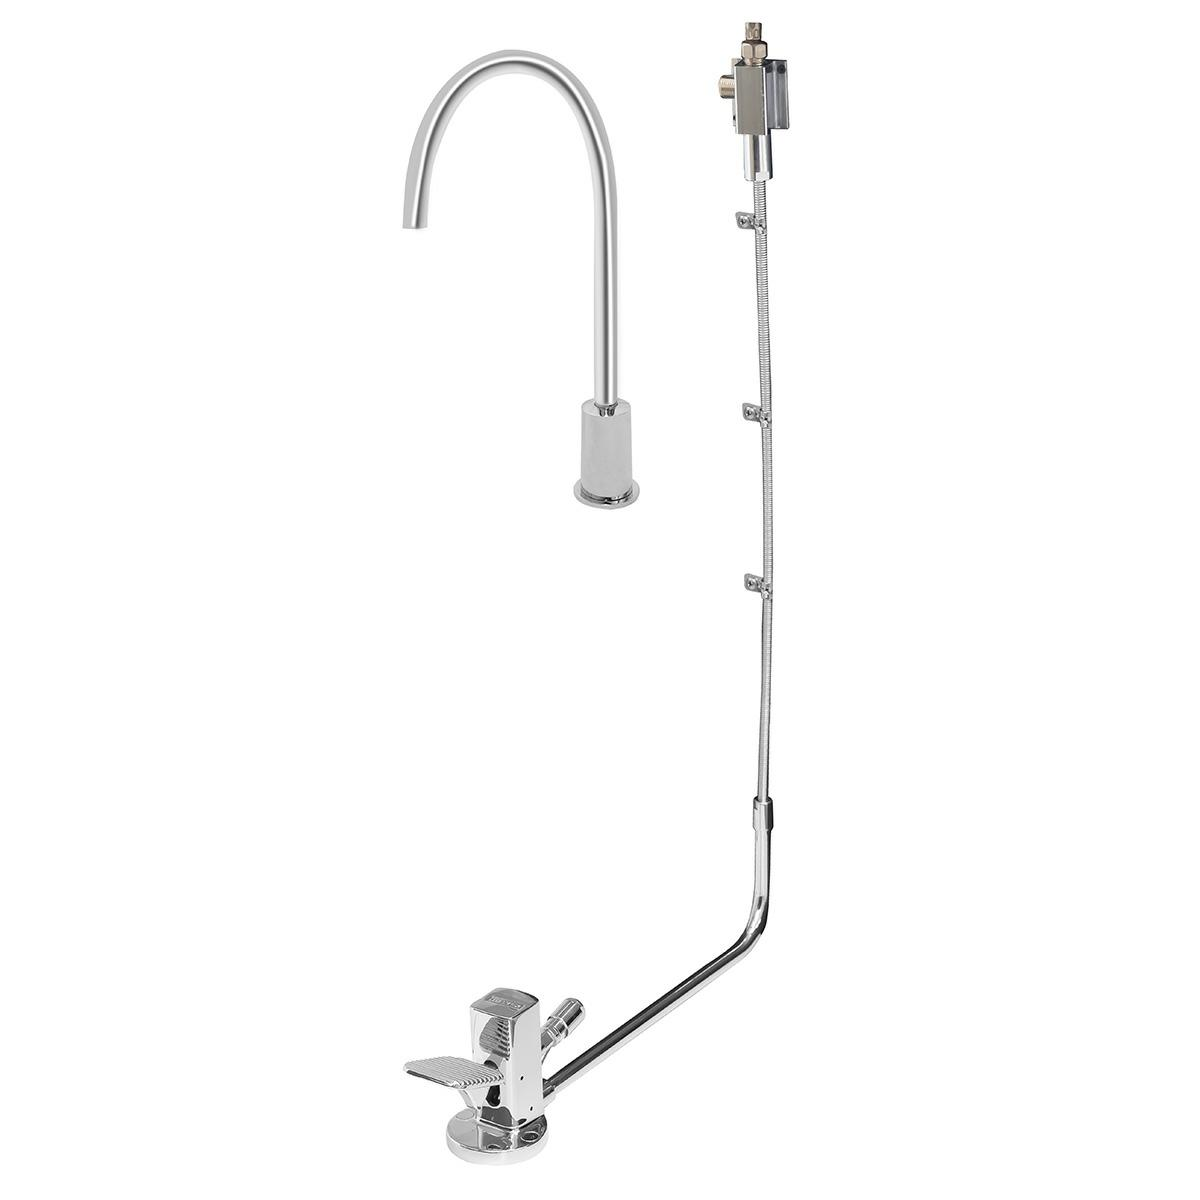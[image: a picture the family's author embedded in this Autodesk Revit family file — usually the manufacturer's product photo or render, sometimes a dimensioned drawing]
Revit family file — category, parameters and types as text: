
# Revit family: VPH-1
name_source: partatom
category: Aparatos sanitarios
units: mm (PartAtom-declared; Revit-internal decimal feet)

## family parameters
Compartido = Sí
Corte con vacíos al cargar = No
Cota de conector redondo = Diámetro de uso
Número OmniClass = 23.45.55.14
Punto de cálculo de habitación = Sí
Se basa en plano de trabajo = Sí
Siempre vertical = Sí
Tipo de pieza = Normal
Título OmniClass = Single Faucets

## types (2) — shared parameters
Accesorios = Conectores ½ -14 NPSM
Cuerpo de Latón = Brass
Elevación por defecto = 1"
Fabricante = HELVEX S.A. de C.V.
Garantía = El producto HELVEX está garantizado como libre de defectos en materiales y procesos de fabricación. El producto HELVEX está garantizado, en lo que se refiere a los acabados; por un periodo de 10 años en los acabados cromo y duravex, y por 2 años en acabados diferentes al cromo, a partir de la fecha de compra indicada en la factura
Hoja Técnica = https://www.helvex.com.mx
Instalación = Conexión ½ - 14 NPSM
Instructivo = https://www.helvex.com.mx
Operación = Para abrir el flujo de agua oprima el pedal con el pie.
Presión Máxima de Trabajo = 85.3 psi
Presión Mínima de Trabajo = 3.6 psi
Total Width = 2"
URL = https://www.helvex.com.mx

## per-type parameters (varying)
| type | Características del Producto | Comentarios de tipo | Descripción | Imagen de tipo | Total Height | Total Lenght |
| VP-2 | Llave para lavabo con pedal expuesto, sin contra | Monomando para lavabo. | Llave para lavabo con pedal expuesto | <Ninguno> | 14" | 8" |
| VPH-1 | Llave para Hospital Cuello de Ganso con Pedal
Expuesto, sin Contra. | Llave para Hospital | Llave de Hospital de Cuello de Ganso Giratorio con Pedal
Expuesto, Cromo | VPH-1.jpg | 16" | 10" |

note: column(s) folded — value = type name in every type: Modelo

## geometry (parser evidence)
native form markers: Sweep x3
no freeform markers — native parametric forms only
